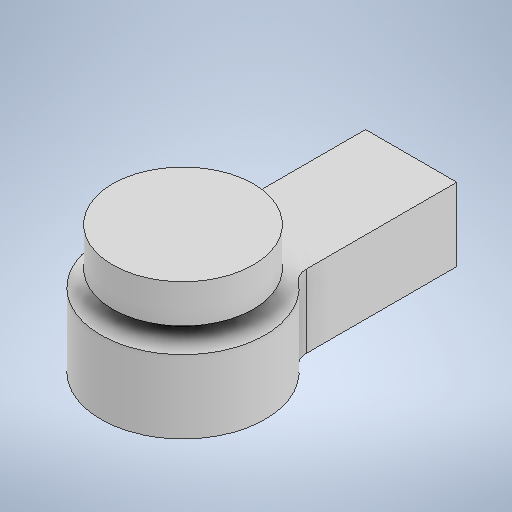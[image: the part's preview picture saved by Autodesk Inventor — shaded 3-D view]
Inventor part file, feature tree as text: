
AUTODESK INVENTOR PART (.ipt)
format: ipt  version: 2025.1 (Build 291241000, 241)  size: 281,088 bytes
history: native  units: mm
features: sketch x2, extrude x1, revolve x1
ambient origin geometry x8: Origin, YZ Plane, XZ Plane, XY Plane, X Axis, Y Axis, Z Axis, Center Point
bodies: Body1 (feature_tree)
feature tree (4):
  extrude  "Extrusion1"  TaperAngle=0.0deg  [1 undecoded]
  revolve  "Umdrehung1"
  sketch  "Skizze1"  dims[d1=18.0mm d2=5.0mm d3=2.0mm d4=4.0mm d5=10.0mm d6=5.0mm d7=0.0mm d8=25.0mm d9=0.0mm]
  sketch  "Skizze3"  dims[d10=0.0mm d11=8.0mm d12=0.0mm d13=6.0mm d14=5.2mm d15=1.0mm d16=1.5mm d17=1.4mm d18=2.8mm d19=90.0deg]
note: 1 required parameter value undecoded (feature->parameter linkage not recoverable at this tier; creation-order binding heuristic only, values carry confidence <= 0.55)
